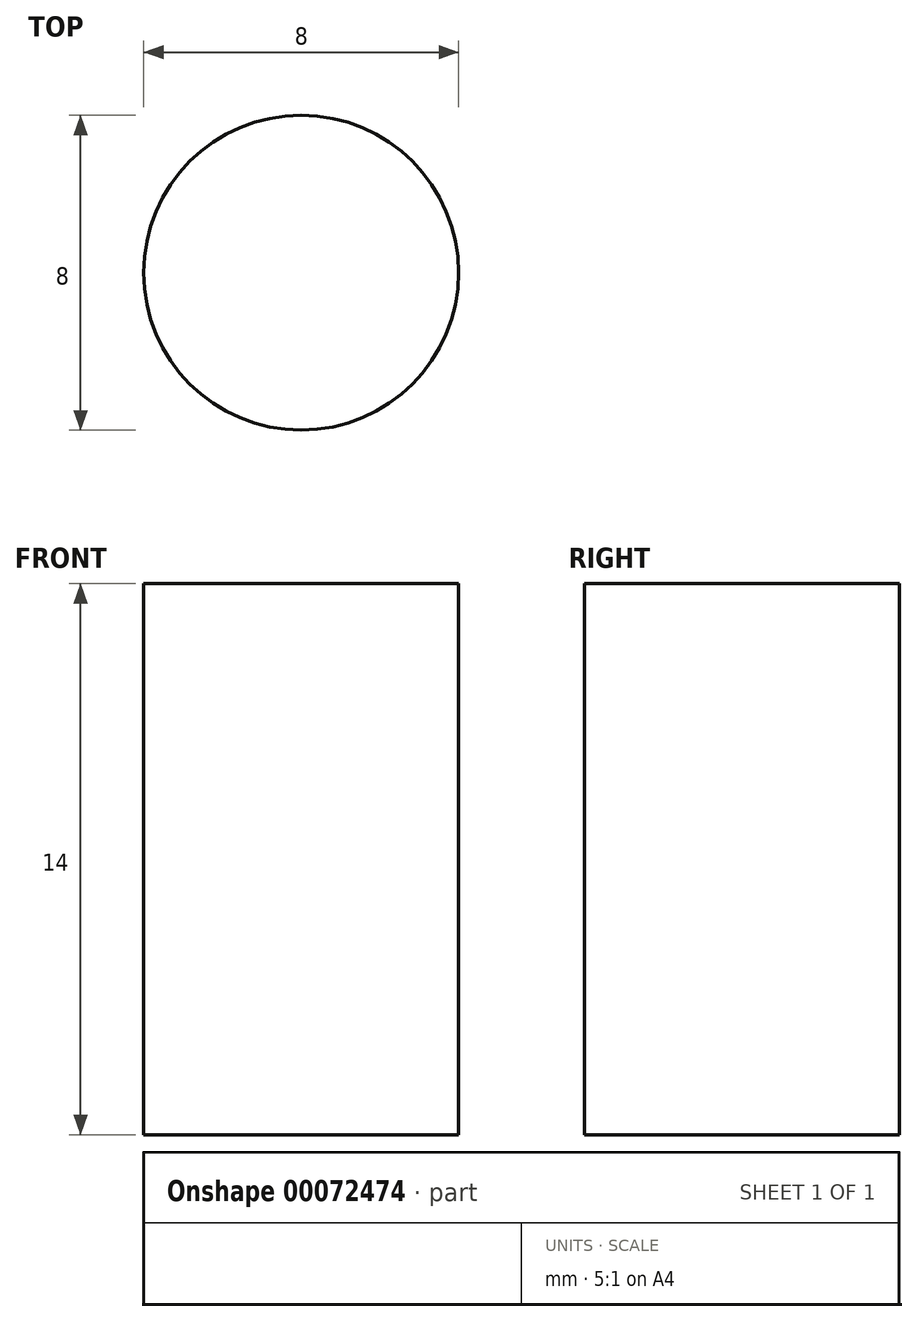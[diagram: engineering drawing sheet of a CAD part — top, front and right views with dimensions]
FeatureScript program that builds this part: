
annotation { "Feature Type Name" : "Feature", "Feature Type Description" : "" }
export const myFeature = defineFeature(function(context is Context, id is Id, definition is map)
    precondition{}
    {
        {
            var Q0;
            Q0=qCreatedBy(makeId("Top.planeOp"),FACE);
            var sketch = newSketch(context, id + "F0", { "sketchPlane" : qUnion([Q0])});
            skCircle(sketch, "E0", {"center": v(0, 0) * mm, "radius": 4 * mm});
            skSolve(sketch);
        }
        {
            var Q0;
            Q0=makeQuery(id+"F0.imprint","IMPRINT",FACE,{"disambiguationData":[TD([[makeQuery(id+"F0.imprint","IMPRINT",EDGE,{"derivedFrom":sQuery(id+"F0.wireOp",EDGE,"E0")}),1.0]])]});
            extrude(context, id + "F1", {"entities" : qUnion([Q0]), "depth" : 14 * mm});
        }
    });
